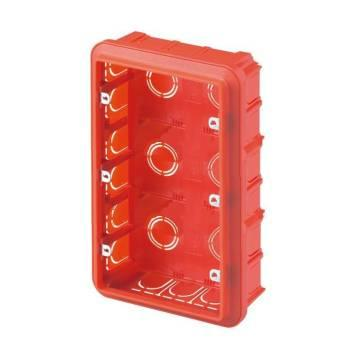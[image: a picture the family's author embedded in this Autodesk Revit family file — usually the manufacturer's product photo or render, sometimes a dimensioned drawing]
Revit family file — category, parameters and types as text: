
# Revit family: Building-ContenitoriIncasso-GEWISS-24SC-SCATOLE-INCASSO_BIGBOX_6P+6P+6P
name_source: partatom
category: Apparecchi elettrici
revit_build: Autodesk Revit 2016 (Build: 20161004_0715(x64)
units: mm (PartAtom-declared; Revit-internal decimal feet)

## family parameters
Condiviso = Sì
Host = Superficie
Mantenere orientamento annotazione = Sì
Numero OmniClass = 23.80.30.14.24
Punto di calcolo locali = Sì
Quota connettore circolare = Usa diametro
Taglio con vuoti quando caricato = Sì
Tipo di parte = Normale
Titolo OmniClass = Junction Boxes

## types (1)
- GW24239 - Scatola 18P (6+6+6)
    Caratteristiche = Halogen free
    Catalogo = BUILDING
    Catalogo Serie = 24SC
    Centro viti = 107 mm  [stored 0.35105 ft]
    Codice EAN = 8011564025004
    Codice Electrocod = 0110
    Descrizione = SCATOLA 18P.(6+6+6) ALTA CAPIENZA
    Descrizione: = 18 posti (6+6+6)
    Dim. esterne BxHxP (mm) = 186x190x65
    Glow Wire Test = 650°C
    IDF = f3ce4417-6700-48c3-bdff-168f39d5d01d
    IDT = ae64a0fb-03f4-4e53-89b4-0a5e4ee210f3
    Immagine tipo = GW24239.jpg
    Installazione = Incasso
    Interasse fissaggio supporti = 163,5MM
    Modello = GW24239
    N. moduli SYSTEM = 18 posti (6+6+6)
    Per Pareti = Muratura
    Predisposizione scomparti = 3
    Produttore = GEWISS S.p.A.
    Prospetto di default = 45 mm  [stored 0.147638 ft]
    SEO = Scatola
    Scheda Tecnica = https://www.gewiss.com
    Temperatura di impiego = -15 +60 °C
    Termopressione con biglia = 70 °C
    Tipo Materiale = Halogen free secondo norma EN 60754-2
    Tipo: = Alta capienza
    URL = https://www.gewiss.com
    Versione file RFA = 19.0

note: [stored X ft] marks values corroborated as IEEE doubles in the binary element streams (Revit-internal decimal feet)
